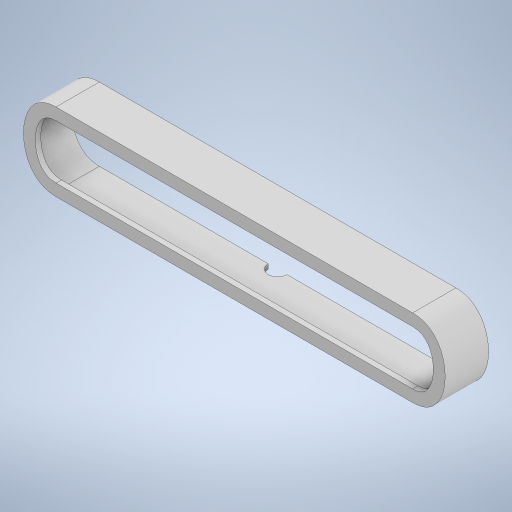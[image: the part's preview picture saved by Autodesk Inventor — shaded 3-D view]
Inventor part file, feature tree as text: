
AUTODESK INVENTOR PART (.ipt)
format: ipt  version: 2023 (Build 270158000, 158)  size: 3,332,608 bytes
history: native  units: in
note: dims shown in document units (in); Inventor stores cm internally (conversion verified against a paired STEP export)
features: extrude x4, other x1
ambient origin geometry x8: Origin, YZ Plane, XZ Plane, XY Plane, X Axis, Y Axis, Z Axis, Center Point
bodies: Solid1 (feature_tree)
feature tree (5):
  extrude  "Extrusion1"  Depth=0.3937in
  extrude  "Extrusion2"  Depth=2.3622in
  extrude  "Extrusion3"  Depth=0.3051in
  extrude  "Extrusion4"  Depth=0.3051in
  other  "Image3"
